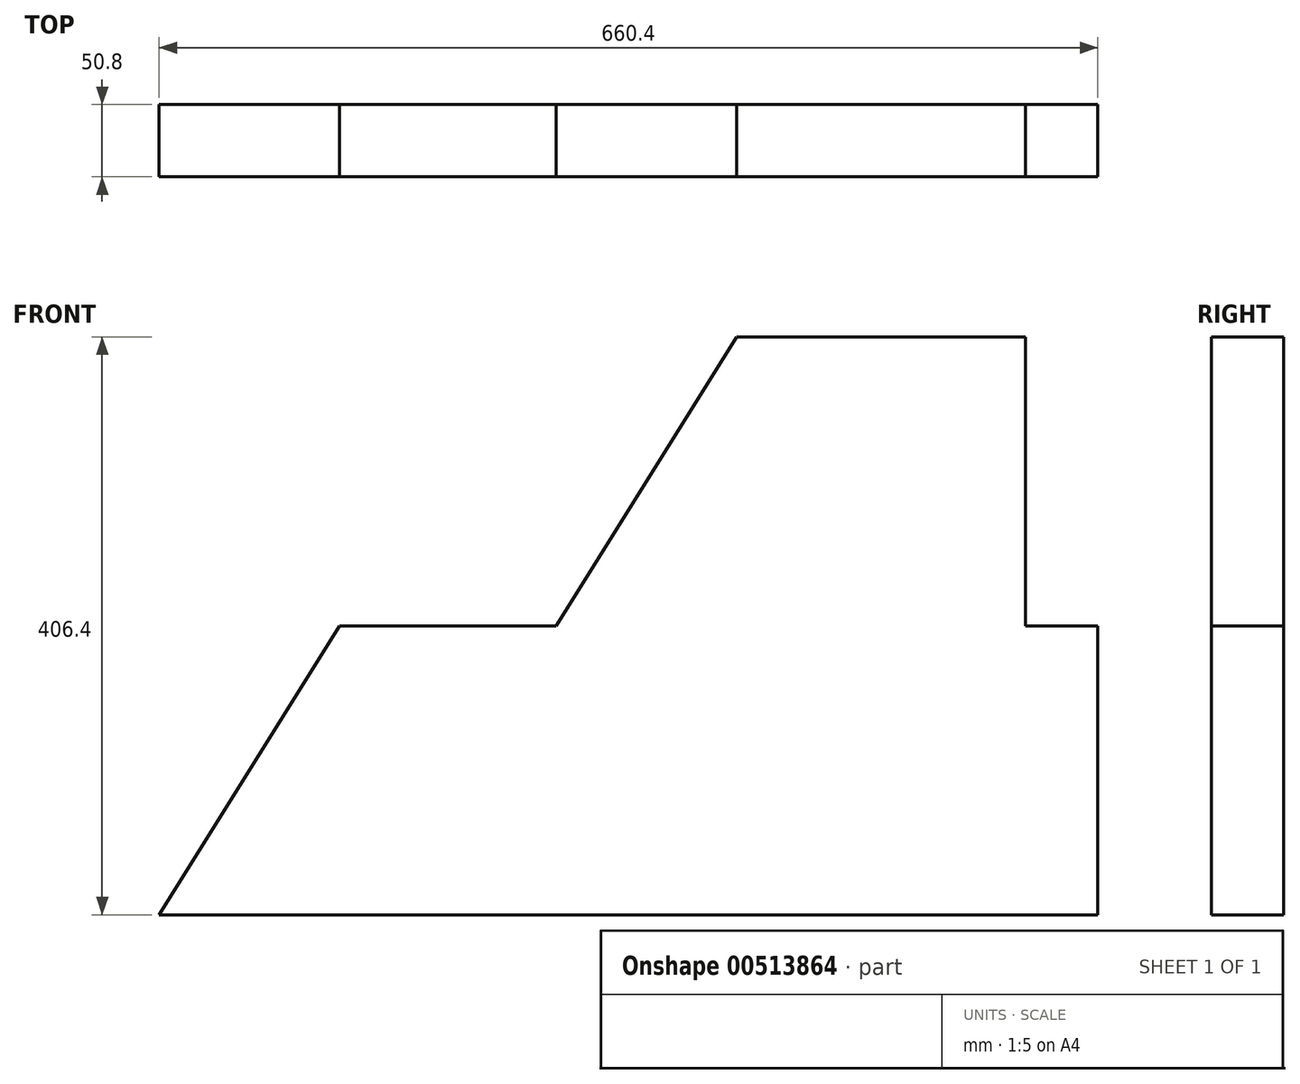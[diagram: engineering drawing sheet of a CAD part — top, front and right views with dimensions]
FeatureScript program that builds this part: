
annotation { "Feature Type Name" : "Feature", "Feature Type Description" : "" }
export const myFeature = defineFeature(function(context is Context, id is Id, definition is map)
    precondition{}
    {
        {
            var Q0;
            Q0=qCreatedBy(makeId("Front.planeOp"),FACE);
            var sketch = newSketch(context, id + "F0", { "sketchPlane" : qUnion([Q0])});
            skLineSegment(sketch, "E0", {"start": v(0, 0) * mm, "end": v(660.4, 0) * mm});
            skLineSegment(sketch, "E1", {"start": v(660.4, 0) * mm, "end": v(660.4, 203.2) * mm});
            skLineSegment(sketch, "E2", {"start": v(660.4, 203.2) * mm, "end": v(609.6, 203.2) * mm});
            skLineSegment(sketch, "E3", {"start": v(609.6, 203.2) * mm, "end": v(609.6, 406.4) * mm});
            skLineSegment(sketch, "E4", {"start": v(609.6, 406.4) * mm, "end": v(406.4, 406.4) * mm});
            skLineSegment(sketch, "E5", {"start": v(406.4, 406.4) * mm, "end": v(279.4, 203.2) * mm});
            skLineSegment(sketch, "E6", {"start": v(279.4, 203.2) * mm, "end": v(127, 203.2) * mm});
            skLineSegment(sketch, "E7", {"start": v(127, 203.2) * mm, "end": v(0, 0) * mm});
            skSolve(sketch);
        }
        {
            var Q0;
            Q0=makeQuery(id+"F0.imprint","IMPRINT",FACE,{"disambiguationData":[TD([[makeQuery(id+"F0.imprint","IMPRINT",EDGE,{"derivedFrom":sQuery(id+"F0.wireOp",EDGE,"E0")}),1.0]])]});
            extrude(context, id + "F1", {"entities" : qUnion([Q0]), "depth" : 50.8 * mm, "offsetDistance" : 25.4 * mm});
        }
    });
